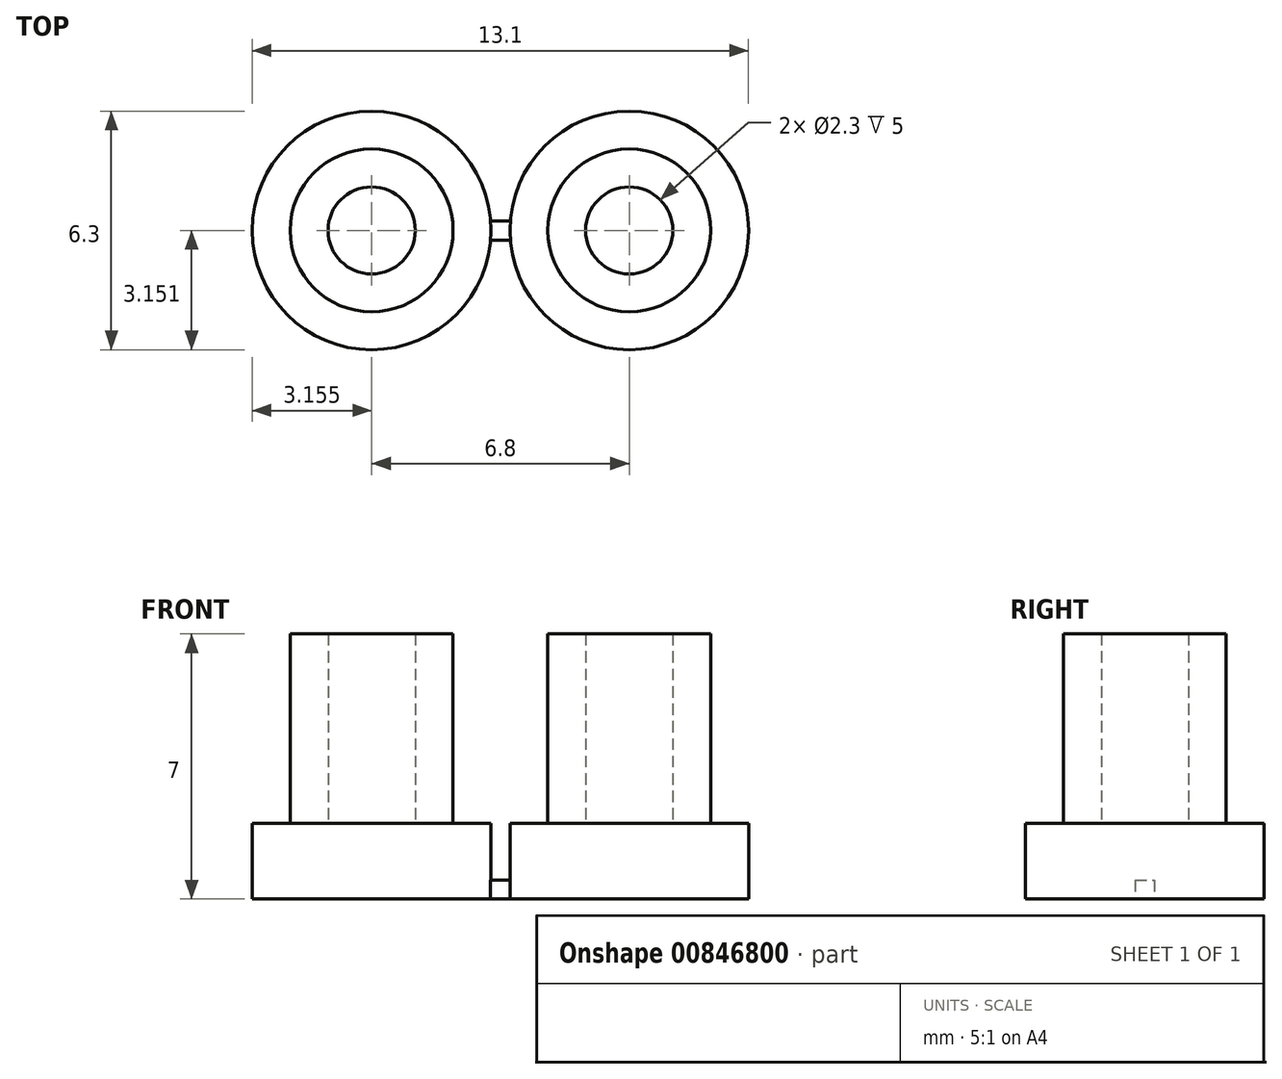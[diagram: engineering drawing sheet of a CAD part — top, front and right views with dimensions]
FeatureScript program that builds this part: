
annotation { "Feature Type Name" : "Feature", "Feature Type Description" : "" }
export const myFeature = defineFeature(function(context is Context, id is Id, definition is map)
    precondition{}
    {
        {
            var Q0;
            Q0=qCreatedBy(makeId("Top.planeOp"),FACE);
            var sketch = newSketch(context, id + "F0", { "sketchPlane" : qUnion([Q0])});
            skCircle(sketch, "E0", {"center": v(-25.03, 19.45) * mm, "radius": 1.15 * mm});
            skCircle(sketch, "E1", {"center": v(-25.03, 19.45) * mm, "radius": 2.15 * mm});
            skCircle(sketch, "E2", {"center": v(-25.03, 19.45) * mm, "radius": 3.15 * mm});
            skCircle(sketch, "E3.1.0.0", {"center": v(-18.23, 19.45) * mm, "radius": 2.15 * mm});
            skCircle(sketch, "E3.1.0.1", {"center": v(-18.23, 19.45) * mm, "radius": 1.15 * mm});
            skCircle(sketch, "E3.1.0.2", {"center": v(-18.23, 19.45) * mm, "radius": 3.15 * mm});
            skLineSegment(sketch, "E3.direction1", {"start": v(-25.03, 19.45) * mm, "end": v(-18.23, 19.45) * mm, "construction": true});
            skPoint(sketch, "E4", {"position": v(-21.88, 19.45) * mm});
            skPoint(sketch, "E5", {"position": v(-21.38, 19.45) * mm});
            skPoint(sketch, "E6", {"position": v(-21.63, 19.45) * mm});
            skLineSegment(sketch, "E7.bottom", {"start": v(-21.37, 19.2) * mm, "end": v(-21.89, 19.2) * mm});
            skLineSegment(sketch, "E7.top", {"start": v(-21.37, 19.7) * mm, "end": v(-21.89, 19.7) * mm});
            skSolve(sketch);
        }
        {
            var Q0;
            Q0=makeQuery(id+"F0.imprint","IMPRINT",FACE,{"disambiguationData":[TD([[makeQuery(id+"F0.imprint","IMPRINT",EDGE,{"derivedFrom":sQuery(id+"F0.wireOp",EDGE,"E0")}),-1.0]])]});
            var Q1;
            Q1=makeQuery(id+"F0.imprint","IMPRINT",FACE,{"disambiguationData":[TD([[makeQuery(id+"F0.imprint","IMPRINT",EDGE,{"derivedFrom":sQuery(id+"F0.wireOp",EDGE,"E3.1.0.0")}),1.0]])]});
            extrude(context, id + "F1", {"entities" : qUnion([Q0, Q1]), "depth" : 7 * mm, "offsetDistance" : 25 * mm});
        }
        {
            var Q0;
            Q0=makeQuery(id+"F0.imprint","IMPRINT",FACE,{"disambiguationData":[TD([[makeQuery(id+"F0.imprint","IMPRINT",EDGE,{"derivedFrom":sQuery(id+"F0.wireOp",EDGE,"E1")}),-1.0]])]});
            var Q1;
            Q1=makeQuery(id+"F0.imprint","IMPRINT",FACE,{"disambiguationData":[TD([[makeQuery(id+"F0.imprint","IMPRINT",EDGE,{"derivedFrom":sQuery(id+"F0.wireOp",EDGE,"E0")}),1.0]])]});
            var Q2;
            Q2=makeQuery(id+"F0.imprint","IMPRINT",FACE,{"disambiguationData":[TD([[makeQuery(id+"F0.imprint","IMPRINT",EDGE,{"derivedFrom":sQuery(id+"F0.wireOp",EDGE,"E3.1.0.0")}),-1.0]])]});
            var Q3;
            Q3=makeQuery(id+"F0.imprint","IMPRINT",FACE,{"disambiguationData":[TD([[makeQuery(id+"F0.imprint","IMPRINT",EDGE,{"derivedFrom":sQuery(id+"F0.wireOp",EDGE,"E3.1.0.1")}),1.0]])]});
            extrude(context, id + "F2", {"entities" : qUnion([Q0, Q1, Q2, Q3]), "operationType" : NewBodyOperationType.ADD, "depth" : 2 * mm, "offsetDistance" : 25 * mm});
        }
        {
            var Q0;
            {var subQ0=sQuery(id+"F0.wireOp",EDGE,"E7.bottom");Q0=makeQuery(id+"F0.imprint","IMPRINT",FACE,{"disambiguationData":[TD([[makeQuery(id+"F0.imprint","IMPRINT",EDGE,{"derivedFrom":subQ0}),-1.0]])]});}
            extrude(context, id + "F3", {"entities" : qUnion([Q0]), "depth" : 0.5 * mm, "offsetDistance" : 25 * mm});
        }
    });
